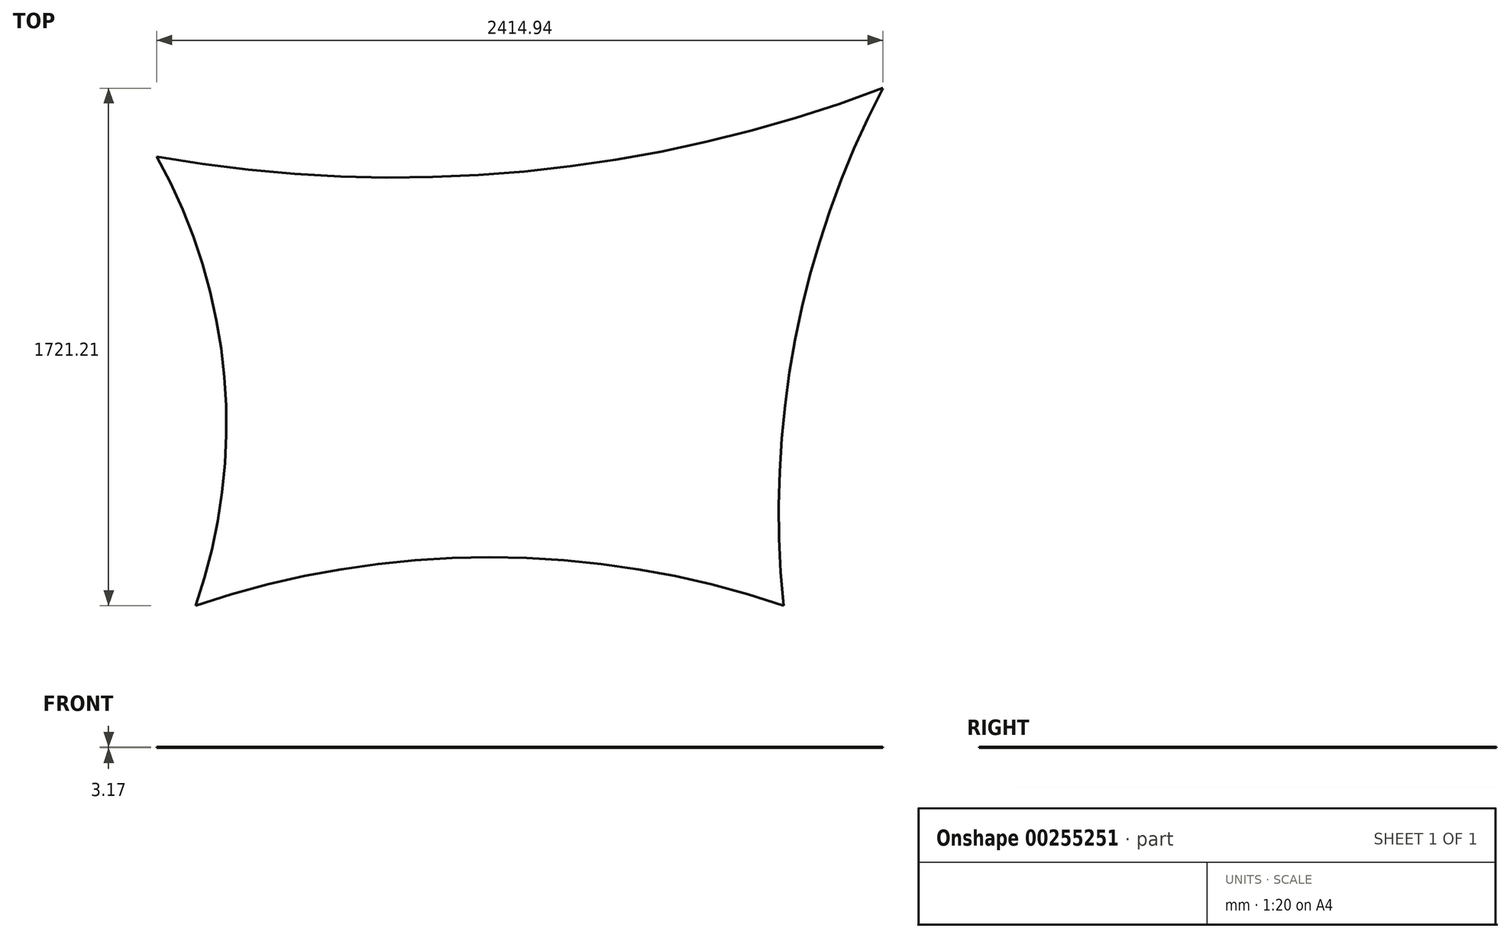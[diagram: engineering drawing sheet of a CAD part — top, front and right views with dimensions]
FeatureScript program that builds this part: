
annotation { "Feature Type Name" : "Feature", "Feature Type Description" : "" }
export const myFeature = defineFeature(function(context is Context, id is Id, definition is map)
    precondition{}
    {
        {
            var Q0;
            Q0=qCreatedBy(makeId("Top.planeOp"),FACE);
            var sketch = newSketch(context, id + "F0", { "sketchPlane" : qUnion([Q0])});
            skPoint(sketch, "E0", {"position": v(0, 0) * mm});
            skPoint(sketch, "E1", {"position": v(-128.94, 1493.04) * mm});
            skPoint(sketch, "E2", {"position": v(1955.8, 0) * mm});
            skPoint(sketch, "E3", {"position": v(2286, 1721.21) * mm});
            skArc(sketch, "E4", {"start": v(0, 0) * mm, "mid": v(95.48, 760.34) * mm, "end": v(-128.94, 1493.04) * mm});
            skArc(sketch, "E5", {"start": v(-128.94, 1493.04) * mm, "mid": v(1093.94, 1444.05) * mm, "end": v(2286, 1721.21) * mm});
            skArc(sketch, "E6", {"start": v(2286, 1721.21) * mm, "mid": v(1994.52, 884.85) * mm, "end": v(1955.8, 0) * mm});
            skArc(sketch, "E7", {"start": v(1955.8, 0) * mm, "mid": v(977.9, 161.13) * mm, "end": v(0, 0) * mm});
            skSolve(sketch);
        }
        {
            var Q0;
            Q0 = qSketchRegion(id + "F0", true);
            extrude(context, id + "F1", {"entities" : qUnion([Q0]), "depth" : 3.17 * mm});
        }
    });
